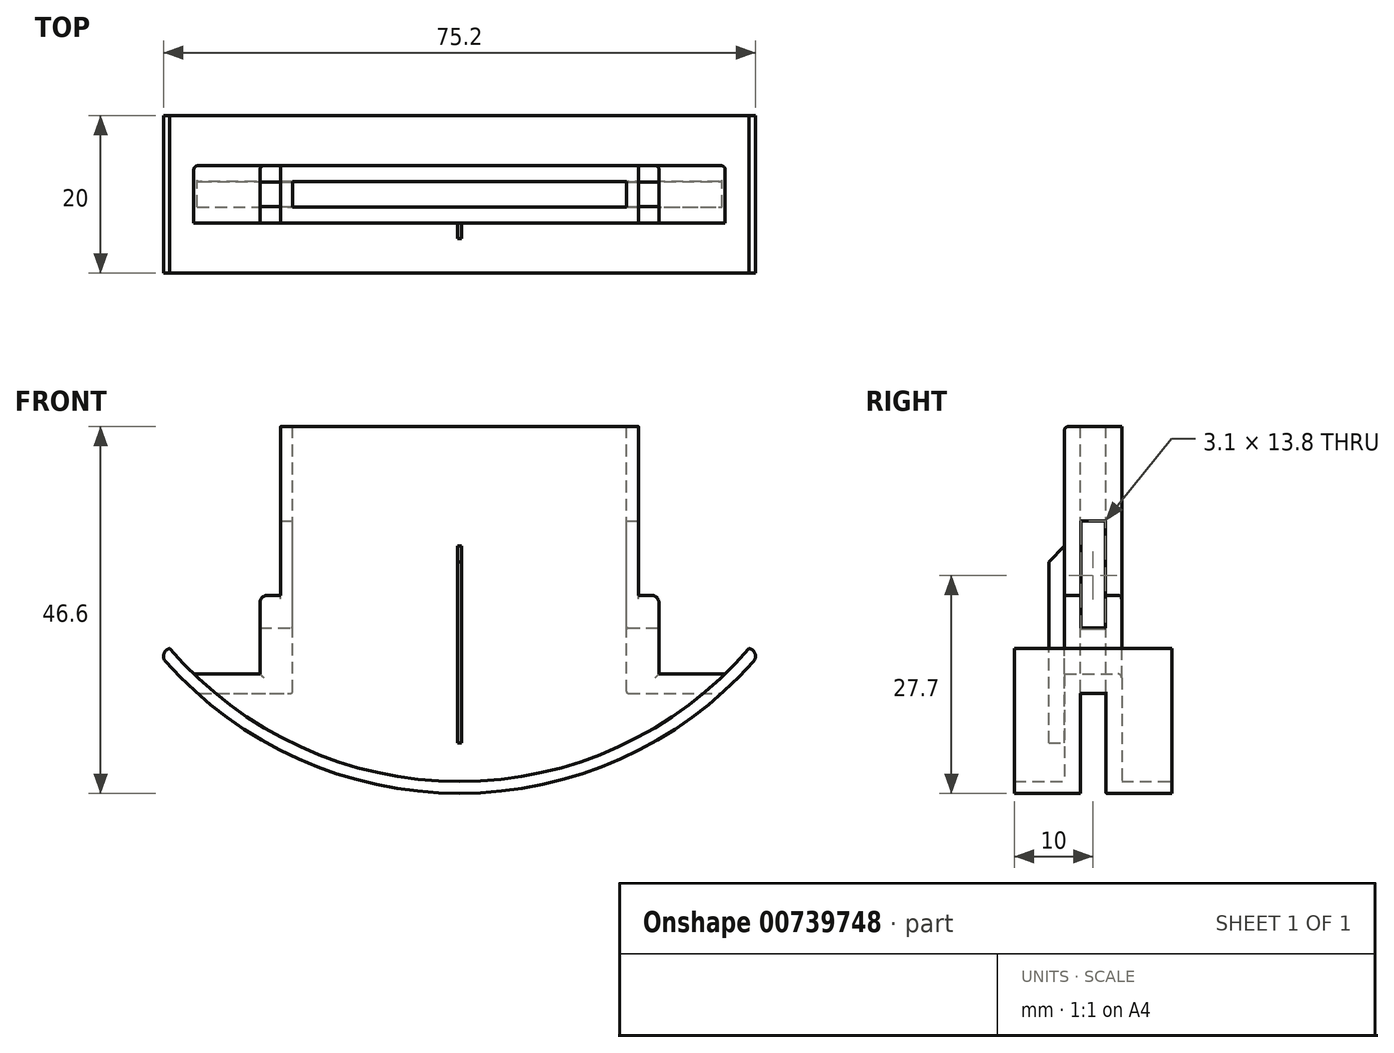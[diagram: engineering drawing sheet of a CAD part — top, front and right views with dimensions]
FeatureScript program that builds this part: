
annotation { "Feature Type Name" : "Feature", "Feature Type Description" : "" }
export const myFeature = defineFeature(function(context is Context, id is Id, definition is map)
    precondition{}
    {
        {
            var Q0;
            Q0=qCreatedBy(makeId("Front.planeOp"),FACE);
            var sketch = newSketch(context, id + "F0", { "sketchPlane" : qUnion([Q0])});
            skArc(sketch, "E0", {"start": v(-38.75, -31.6) * mm, "mid": v(0, -50) * mm, "end": v(38.75, -31.6) * mm});
            skArc(sketch, "E1", {"start": v(-36.8, -31.6) * mm, "mid": v(0, -48.5) * mm, "end": v(36.8, -31.6) * mm});
            skLineSegment(sketch, "E2", {"start": v(-38.75, -31.6) * mm, "end": v(-36.8, -31.6) * mm});
            skLineSegment(sketch, "E3.MirrorCS", {"start": v(38.75, -31.6) * mm, "end": v(36.8, -31.6) * mm});
            skSolve(sketch);
        }
        {
            var Q0;
            Q0 = qSketchRegion(id + "F0", true);
            extrude(context, id + "F1", {"entities" : qUnion([Q0]), "depth" : 20 * mm, "offsetDistance" : 25 * mm});
        }
        {
            var Q0;
            Q0=qCreatedBy(makeId("Top.planeOp"),FACE);
            var sketch = newSketch(context, id + "F2", { "sketchPlane" : qUnion([Q0])});
            skLineSegment(sketch, "E4", {"start": v(-40.45, -10) * mm, "end": v(40.4, -10) * mm, "construction": true});
            skLineSegment(sketch, "E5.bottom", {"start": v(-33.75, -6.37) * mm, "end": v(33.75, -6.37) * mm});
            skLineSegment(sketch, "E5.top", {"start": v(-33.75, -13.63) * mm, "end": v(33.75, -13.63) * mm});
            skLineSegment(sketch, "E5.left", {"start": v(-33.75, -6.37) * mm, "end": v(-33.75, -13.63) * mm});
            skLineSegment(sketch, "E5.right", {"start": v(33.75, -6.37) * mm, "end": v(33.75, -13.63) * mm});
            skSolve(sketch);
        }
        {
            var Q0;
            Q0 = qSketchRegion(id + "F2", true);
            extrude(context, id + "F3", {"entities" : qUnion([Q0]), "operationType" : NewBodyOperationType.ADD, "oppositeDirection" : true, "depth" : 48.69 * mm, "offsetDistance" : 25 * mm});
        }
        {
            var Q0;
            Q0=makeQuery(id+"F3.opExtrude","CAP_FACE",FACE,{"disambiguationData":[OSD([sQuery(id+"F2.wireOp",EDGE,"E5.bottom"),sQuery(id+"F2.wireOp",EDGE,"E5.top"),sQuery(id+"F2.wireOp",EDGE,"E5.left"),sQuery(id+"F2.wireOp",EDGE,"E5.right")])],"isStart":true});
            var sketch = newSketch(context, id + "F4", { "sketchPlane" : qUnion([Q0])});
            skLineSegment(sketch, "E6", {"start": v(-42.86, -10) * mm, "end": v(43.1, -10) * mm, "construction": true});
            skPoint(sketch, "E6.startSnap0", {"position": v(-33.75, -10) * mm});
            skLineSegment(sketch, "E7.0", {"start": v(-33.75, -6.37) * mm, "end": v(33.75, -6.37) * mm});
            skLineSegment(sketch, "E8.0", {"start": v(-36.8, 0) * mm, "end": v(36.8, 0) * mm});
            skLineSegment(sketch, "E9.bottom", {"start": v(-21.2, -8.4) * mm, "end": v(21.2, -8.4) * mm});
            skLineSegment(sketch, "E9.top", {"start": v(-21.2, -11.6) * mm, "end": v(21.2, -11.6) * mm});
            skLineSegment(sketch, "E9.left", {"start": v(-21.2, -8.4) * mm, "end": v(-21.2, -11.6) * mm});
            skLineSegment(sketch, "E9.right", {"start": v(21.2, -8.4) * mm, "end": v(21.2, -11.6) * mm});
            skSolve(sketch);
        }
        {
            var Q0;
            Q0 = qSketchRegion(id + "F4", true);
            extrude(context, id + "F5", {"entities" : qUnion([Q0]), "operationType" : NewBodyOperationType.REMOVE, "endBound" : BoundingType.THROUGH_ALL, "oppositeDirection" : true, "depth" : 25 * mm, "offsetDistance" : 25 * mm});
        }
        {
            var Q0;
            {var subQ0=sQuery(id+"F2.wireOp",EDGE,"E5.left");var subQ1=sQuery(id+"F2.wireOp",EDGE,"E5.bottom");Q0=makeQuery(id+"F3.boolean.opBoolean","SPLIT",FACE,{"disambiguationData":[TD([makeQuery(id+"F1.opExtrude","SWEPT_FACE",FACE,{"disambiguationData":[OSD([sQuery(id+"F0.wireOp",EDGE,"E0")])]}),makeQuery(id+"F3.opExtrude","CAP_FACE",FACE,{"disambiguationData":[OSD([subQ1,sQuery(id+"F2.wireOp",EDGE,"E5.top"),subQ0,sQuery(id+"F2.wireOp",EDGE,"E5.right")])],"isStart":false}),makeQuery(id+"F3.opExtrude","SWEPT_FACE",FACE,{"disambiguationData":[OSD([subQ0])]})])],"derivedFrom":makeQuery(id+"F3.opExtrude","SWEPT_FACE",FACE,{"disambiguationData":[OSD([subQ1])]})});}
            var sketch = newSketch(context, id + "F6", { "sketchPlane" : qUnion([Q0])});
            skLineSegment(sketch, "E10.0.0", {"start": v(33.75, -48.69) * mm, "end": v(33.75, -36.9) * mm});
            skArc(sketch, "E10.0.1", {"start": v(33.75, -36.9) * mm, "mid": v(23.32, -44.23) * mm, "end": v(11.37, -48.69) * mm});
            skLineSegment(sketch, "E10.0.2", {"start": v(11.37, -48.69) * mm, "end": v(33.75, -48.69) * mm});
            skLineSegment(sketch, "E11.0.0", {"start": v(-33.75, -48.69) * mm, "end": v(-11.37, -48.69) * mm});
            skArc(sketch, "E11.0.1", {"start": v(-11.37, -48.69) * mm, "mid": v(-23.32, -44.23) * mm, "end": v(-33.75, -36.9) * mm});
            skLineSegment(sketch, "E11.0.2", {"start": v(-33.75, -36.9) * mm, "end": v(-33.75, -48.69) * mm});
            skSolve(sketch);
        }
        {
            var Q0;
            Q0 = qSketchRegion(id + "F6", true);
            extrude(context, id + "F7", {"entities" : qUnion([Q0]), "operationType" : NewBodyOperationType.REMOVE, "endBound" : BoundingType.THROUGH_ALL, "oppositeDirection" : true, "depth" : 25 * mm, "offsetDistance" : 25 * mm});
        }
        {
            var Q0;
            {var subQ0=sQuery(id+"F2.wireOp",EDGE,"E5.right");var subQ1=sQuery(id+"F2.wireOp",EDGE,"E5.left");var subQ2=sQuery(id+"F2.wireOp",EDGE,"E5.bottom");Q0=makeQuery(id+"F3.boolean.opBoolean","SPLIT",FACE,{"disambiguationData":[TD([makeQuery(id+"F1.opExtrude","SWEPT_FACE",FACE,{"disambiguationData":[OSD([sQuery(id+"F0.wireOp",EDGE,"E1")])]}),makeQuery(id+"F3.opExtrude","CAP_FACE",FACE,{"disambiguationData":[OSD([subQ2,sQuery(id+"F2.wireOp",EDGE,"E5.top"),subQ1,subQ0])],"isStart":true}),makeQuery(id+"F3.opExtrude","SWEPT_FACE",FACE,{"disambiguationData":[OSD([subQ1])]}),makeQuery(id+"F3.opExtrude","SWEPT_FACE",FACE,{"disambiguationData":[OSD([subQ0])]})])],"derivedFrom":makeQuery(id+"F3.opExtrude","SWEPT_FACE",FACE,{"disambiguationData":[OSD([subQ2])]})});}
            var sketch = newSketch(context, id + "F8", { "sketchPlane" : qUnion([Q0])});
            skLineSegment(sketch, "E12.0", {"start": v(33.75, 0) * mm, "end": v(-33.75, 0) * mm});
            skArc(sketch, "E13.0", {"start": v(38.75, -31.6) * mm, "mid": v(0, -50) * mm, "end": v(-38.75, -31.6) * mm});
            skLineSegment(sketch, "E14.bottom", {"start": v(-33.75, 0) * mm, "end": v(33.75, 0) * mm});
            skLineSegment(sketch, "E14.top", {"start": v(-33.75, -3.4) * mm, "end": v(33.75, -3.4) * mm});
            skLineSegment(sketch, "E14.left", {"start": v(-33.75, 0) * mm, "end": v(-33.75, -3.4) * mm});
            skLineSegment(sketch, "E14.right", {"start": v(33.75, 0) * mm, "end": v(33.75, -3.4) * mm});
            skSolve(sketch);
        }
        {
            var Q0;
            Q0 = qSketchRegion(id + "F8", true);
            extrude(context, id + "F9", {"entities" : qUnion([Q0]), "operationType" : NewBodyOperationType.REMOVE, "endBound" : BoundingType.THROUGH_ALL, "oppositeDirection" : true, "depth" : 25 * mm, "offsetDistance" : 25 * mm});
        }
        {
            var Q0;
            {var subQ1=sQuery(id+"F2.wireOp",EDGE,"E5.right");Q0=makeQuery(id+"F3.boolean.opBoolean","SPLIT",FACE,{"disambiguationData":[TD([makeQuery(id+"F1.opExtrude","SWEPT_FACE",FACE,{"disambiguationData":[OSD([sQuery(id+"F0.wireOp",EDGE,"E1")])]})])],"derivedFrom":makeQuery(id+"F3.opExtrude","SWEPT_FACE",FACE,{"disambiguationData":[OSD([subQ1])]})});}
            var sketch = newSketch(context, id + "F10", { "sketchPlane" : qUnion([Q0])});
            skLineSegment(sketch, "E15.bottom", {"start": v(-11.55, -15.4) * mm, "end": v(-8.45, -15.4) * mm});
            skLineSegment(sketch, "E15.top", {"start": v(-11.55, -29) * mm, "end": v(-8.45, -29) * mm});
            skLineSegment(sketch, "E15.left", {"start": v(-11.55, -15.4) * mm, "end": v(-11.55, -29) * mm});
            skLineSegment(sketch, "E15.right", {"start": v(-8.45, -15.4) * mm, "end": v(-8.45, -29) * mm});
            skLineSegment(sketch, "E16.0", {"start": v(-13.63, -3.4) * mm, "end": v(-6.37, -3.4) * mm});
            skLineSegment(sketch, "E17.0", {"start": v(-13.63, -34.83) * mm, "end": v(-13.63, -3.4) * mm});
            skLineSegment(sketch, "E18.0", {"start": v(-6.37, -34.83) * mm, "end": v(-6.37, -3.4) * mm});
            skLineSegment(sketch, "E19", {"start": v(-10, -53.79) * mm, "end": v(-10, 8.71) * mm, "construction": true});
            skSolve(sketch);
        }
        {
            var Q0;
            Q0 = qSketchRegion(id + "F10", true);
            extrude(context, id + "F11", {"entities" : qUnion([Q0]), "operationType" : NewBodyOperationType.REMOVE, "endBound" : BoundingType.THROUGH_ALL, "oppositeDirection" : true, "depth" : 25 * mm, "offsetDistance" : 25 * mm});
        }
        {
            var Q0;
            {var subQ0=sQuery(id+"F2.wireOp",EDGE,"E5.right");var subQ1=sQuery(id+"F2.wireOp",EDGE,"E5.left");var subQ2=sQuery(id+"F2.wireOp",EDGE,"E5.top");Q0=makeQuery(id+"F3.boolean.opBoolean","SPLIT",FACE,{"disambiguationData":[TD([makeQuery(id+"F1.opExtrude","SWEPT_FACE",FACE,{"disambiguationData":[OSD([sQuery(id+"F0.wireOp",EDGE,"E1")])]}),makeQuery(id+"F3.opExtrude","CAP_FACE",FACE,{"disambiguationData":[OSD([sQuery(id+"F2.wireOp",EDGE,"E5.bottom"),subQ2,subQ1,subQ0])],"isStart":true}),makeQuery(id+"F3.opExtrude","SWEPT_FACE",FACE,{"disambiguationData":[OSD([subQ1])]}),makeQuery(id+"F3.opExtrude","SWEPT_FACE",FACE,{"disambiguationData":[OSD([subQ0])]})])],"derivedFrom":makeQuery(id+"F3.opExtrude","SWEPT_FACE",FACE,{"disambiguationData":[OSD([subQ2])]})});}
            var sketch = newSketch(context, id + "F12", { "sketchPlane" : qUnion([Q0])});
            skLineSegment(sketch, "E20.0", {"start": v(-33.75, -34.83) * mm, "end": v(-33.75, -3.4) * mm});
            skLineSegment(sketch, "E21", {"start": v(-33.75, -34.83) * mm, "end": v(-25.35, -34.83) * mm});
            skLineSegment(sketch, "E22", {"start": v(-25.35, -34.83) * mm, "end": v(-25.35, -24.83) * mm});
            skLineSegment(sketch, "E23", {"start": v(-25.35, -24.83) * mm, "end": v(-22.75, -24.83) * mm});
            skLineSegment(sketch, "E24", {"start": v(-22.75, -24.83) * mm, "end": v(-22.75, -3.4) * mm});
            skLineSegment(sketch, "E25", {"start": v(-33.75, -3.4) * mm, "end": v(-22.75, -3.4) * mm});
            skLineSegment(sketch, "E26.MirrorCS", {"start": v(33.75, -34.83) * mm, "end": v(33.75, -3.4) * mm});
            skLineSegment(sketch, "E27.MirrorCS", {"start": v(33.75, -34.83) * mm, "end": v(25.35, -34.83) * mm});
            skLineSegment(sketch, "E28.MirrorCS", {"start": v(25.35, -34.83) * mm, "end": v(25.35, -24.83) * mm});
            skLineSegment(sketch, "E29.MirrorCS", {"start": v(22.75, -24.83) * mm, "end": v(22.75, -3.4) * mm});
            skLineSegment(sketch, "E30.MirrorCS", {"start": v(25.35, -24.83) * mm, "end": v(22.75, -24.83) * mm});
            skLineSegment(sketch, "E31.MirrorCS", {"start": v(33.75, -3.4) * mm, "end": v(22.75, -3.4) * mm});
            skSolve(sketch);
        }
        {
            var Q0;
            Q0 = qSketchRegion(id + "F12", true);
            extrude(context, id + "F13", {"entities" : qUnion([Q0]), "operationType" : NewBodyOperationType.REMOVE, "endBound" : BoundingType.THROUGH_ALL, "oppositeDirection" : true, "depth" : 25 * mm, "offsetDistance" : 25 * mm});
        }
        {
            var Q0;
            Q0=qCreatedBy(makeId("Right.planeOp"),FACE);
            cPlane(context, id + "F14", {"entities" : qUnion([Q0]), "cplaneType" : CPlaneType.OFFSET, "offset" : 35 * mm, "width" : 150 * mm, "height" : 150 * mm});
        }
        {
            var Q0;
            Q0=qCreatedBy(id+"F14.planeOp",FACE);
            var sketch = newSketch(context, id + "F15", { "sketchPlane" : qUnion([Q0])});
            skPoint(sketch, "E32.0", {"position": v(-11.6, -45.28) * mm});
            skPoint(sketch, "E33.0", {"position": v(-8.4, -45.28) * mm});
            skLineSegment(sketch, "E34.bottom", {"start": v(-11.6, -45.28) * mm, "end": v(-8.4, -45.28) * mm});
            skLineSegment(sketch, "E34.top", {"start": v(-11.6, -37.28) * mm, "end": v(-8.4, -37.28) * mm});
            skLineSegment(sketch, "E34.left", {"start": v(-11.6, -45.28) * mm, "end": v(-11.6, -37.28) * mm});
            skLineSegment(sketch, "E34.right", {"start": v(-8.4, -45.28) * mm, "end": v(-8.4, -37.28) * mm});
            skSolve(sketch);
        }
        {
            var Q0;
            Q0 = qSketchRegion(id + "F15", true);
            extrude(context, id + "F16", {"entities" : qUnion([Q0]), "operationType" : NewBodyOperationType.REMOVE, "endBound" : BoundingType.THROUGH_ALL, "oppositeDirection" : true, "depth" : 25 * mm, "offsetDistance" : 25 * mm});
        }
        {
            var Q0;
            {var subQ0=sQuery(id+"F2.wireOp",EDGE,"E5.right");var subQ1=sQuery(id+"F2.wireOp",EDGE,"E5.left");var subQ2=sQuery(id+"F2.wireOp",EDGE,"E5.top");Q0=makeQuery(id+"F3.boolean.opBoolean","SPLIT",FACE,{"disambiguationData":[TD([makeQuery(id+"F1.opExtrude","SWEPT_FACE",FACE,{"disambiguationData":[OSD([sQuery(id+"F0.wireOp",EDGE,"E1")])]}),makeQuery(id+"F3.opExtrude","CAP_FACE",FACE,{"disambiguationData":[OSD([sQuery(id+"F2.wireOp",EDGE,"E5.bottom"),subQ2,subQ1,subQ0])],"isStart":true}),makeQuery(id+"F3.opExtrude","SWEPT_FACE",FACE,{"disambiguationData":[OSD([subQ1])]}),makeQuery(id+"F3.opExtrude","SWEPT_FACE",FACE,{"disambiguationData":[OSD([subQ0])]})])],"derivedFrom":makeQuery(id+"F3.opExtrude","SWEPT_FACE",FACE,{"disambiguationData":[OSD([subQ2])]})});}
            var sketch = newSketch(context, id + "F17", { "sketchPlane" : qUnion([Q0])});
            skLineSegment(sketch, "E35.bottom", {"start": v(-0.25, -43.58) * mm, "end": v(0.25, -43.58) * mm});
            skLineSegment(sketch, "E35.top", {"start": v(-0.25, -18.58) * mm, "end": v(0.25, -18.58) * mm});
            skLineSegment(sketch, "E35.left", {"start": v(-0.25, -43.58) * mm, "end": v(-0.25, -18.58) * mm});
            skLineSegment(sketch, "E35.right", {"start": v(0.25, -43.58) * mm, "end": v(0.25, -18.58) * mm});
            skSolve(sketch);
        }
        {
            var Q0;
            Q0 = qSketchRegion(id + "F17", true);
            extrude(context, id + "F18", {"entities" : qUnion([Q0]), "operationType" : NewBodyOperationType.ADD, "depth" : 2 * mm, "offsetDistance" : 25 * mm});
        }
        {
            var Q0;
            Q0=makeQuery(id+"F18.opExtrude","CAP_EDGE",EDGE,{"disambiguationData":[OSD([sQuery(id+"F17.wireOp",EDGE,"E35.top")])],"isStart":false});
            chamfer(context, id + "F19", {"entities" : qUnion([Q0]), "width" : 2 * mm, "tangentPropagation" : true});
        }
        {
            var Q0;
            Q0=makeQuery(id+"F13.boolean.opBoolean","COPY",EDGE,{"derivedFrom":makeQuery(id+"F13.opExtrude","SWEPT_EDGE",EDGE,{"disambiguationData":[OSD([sQuery(id+"F2.wireOp",EDGE,"E5.top"),sQuery(id+"F8.wireOp",EDGE,"E14.top"),sQuery(id+"F12.wireOp",EDGE,"E29.MirrorCS"),sQuery(id+"F12.wireOp",EDGE,"E31.MirrorCS")])]})});
            var Q1;
            Q1=makeQuery(id+"F13.boolean.opBoolean","COPY",EDGE,{"derivedFrom":makeQuery(id+"F13.opExtrude","SWEPT_EDGE",EDGE,{"disambiguationData":[OSD([sQuery(id+"F2.wireOp",EDGE,"E5.top"),sQuery(id+"F8.wireOp",EDGE,"E14.top"),sQuery(id+"F12.wireOp",EDGE,"E24"),sQuery(id+"F12.wireOp",EDGE,"E25")])]})});
            var Q2;
            {var subQ0=sQuery(id+"F12.wireOp",EDGE,"E28.MirrorCS");var subQ1=sQuery(id+"F12.wireOp",EDGE,"E30.MirrorCS");Q2=makeQuery(id+"F13.boolean.opBoolean","COPY",EDGE,{"disambiguationData":[TD([makeQuery(id+"F3.opExtrude","SWEPT_FACE",FACE,{"disambiguationData":[OSD([sQuery(id+"F2.wireOp",EDGE,"E5.bottom")])]})])],"derivedFrom":makeQuery(id+"F13.opExtrude","SWEPT_EDGE",EDGE,{"disambiguationData":[OSD([subQ0,subQ1])]})});}
            var Q3;
            {var subQ0=sQuery(id+"F12.wireOp",EDGE,"E28.MirrorCS");var subQ1=sQuery(id+"F12.wireOp",EDGE,"E30.MirrorCS");Q3=makeQuery(id+"F13.boolean.opBoolean","COPY",EDGE,{"disambiguationData":[TD([makeQuery(id+"F3.opExtrude","SWEPT_FACE",FACE,{"disambiguationData":[OSD([sQuery(id+"F2.wireOp",EDGE,"E5.top")])]})])],"derivedFrom":makeQuery(id+"F13.opExtrude","SWEPT_EDGE",EDGE,{"disambiguationData":[OSD([subQ0,subQ1])]})});}
            var Q4;
            {var subQ0=sQuery(id+"F12.wireOp",EDGE,"E23");var subQ1=sQuery(id+"F12.wireOp",EDGE,"E22");Q4=makeQuery(id+"F13.boolean.opBoolean","COPY",EDGE,{"disambiguationData":[TD([makeQuery(id+"F3.opExtrude","SWEPT_FACE",FACE,{"disambiguationData":[OSD([sQuery(id+"F2.wireOp",EDGE,"E5.bottom")])]})])],"derivedFrom":makeQuery(id+"F13.opExtrude","SWEPT_EDGE",EDGE,{"disambiguationData":[OSD([subQ1,subQ0])]})});}
            var Q5;
            {var subQ0=sQuery(id+"F12.wireOp",EDGE,"E22");var subQ1=sQuery(id+"F12.wireOp",EDGE,"E23");Q5=makeQuery(id+"F13.boolean.opBoolean","COPY",EDGE,{"disambiguationData":[TD([makeQuery(id+"F3.opExtrude","SWEPT_FACE",FACE,{"disambiguationData":[OSD([sQuery(id+"F2.wireOp",EDGE,"E5.top")])]})])],"derivedFrom":makeQuery(id+"F13.opExtrude","SWEPT_EDGE",EDGE,{"disambiguationData":[OSD([subQ0,subQ1])]})});}
            var Q6;
            Q6=makeQuery(id+"F1.opExtrude","SWEPT_EDGE",EDGE,{"disambiguationData":[OSD([sQuery(id+"F0.wireOp",EDGE,"E0"),sQuery(id+"F0.wireOp",EDGE,"E2")])]});
            var Q7;
            Q7=makeQuery(id+"F1.opExtrude","SWEPT_EDGE",EDGE,{"disambiguationData":[OSD([sQuery(id+"F0.wireOp",EDGE,"E0"),sQuery(id+"F0.wireOp",EDGE,"E3.MirrorCS")])]});
            fillet(context, id + "F20", {"entities" : qUnion([Q0, Q1, Q2, Q3, Q4, Q5, Q6, Q7]), "radius" : 1 * mm, "tangentPropagation" : true, "allowEdgeOverflow" : false});
        }
        {
            var Q0;
            Q0=makeQuery(id+"F9.boolean.opBoolean","COPY",EDGE,{"derivedFrom":makeQuery(id+"F9.opExtrude","CAP_EDGE",EDGE,{"disambiguationData":[OSD([sQuery(id+"F8.wireOp",EDGE,"E14.top")])],"isStart":true})});
            var Q1;
            {var subQ0=sQuery(id+"F2.wireOp",EDGE,"E5.right");var subQ1=sQuery(id+"F2.wireOp",EDGE,"E5.left");var subQ2=sQuery(id+"F2.wireOp",EDGE,"E5.top");Q1=makeQuery(id+"F9.boolean.opBoolean","INTERSECT",EDGE,{"derivedFrom":[makeQuery(id+"F3.boolean.opBoolean","SPLIT",FACE,{"disambiguationData":[TD([makeQuery(id+"F1.opExtrude","SWEPT_FACE",FACE,{"disambiguationData":[OSD([sQuery(id+"F0.wireOp",EDGE,"E1")])]}),makeQuery(id+"F3.opExtrude","CAP_FACE",FACE,{"disambiguationData":[OSD([sQuery(id+"F2.wireOp",EDGE,"E5.bottom"),subQ2,subQ1,subQ0])],"isStart":true}),makeQuery(id+"F3.opExtrude","SWEPT_FACE",FACE,{"disambiguationData":[OSD([subQ1])]}),makeQuery(id+"F3.opExtrude","SWEPT_FACE",FACE,{"disambiguationData":[OSD([subQ0])]})])],"derivedFrom":makeQuery(id+"F3.opExtrude","SWEPT_FACE",FACE,{"disambiguationData":[OSD([subQ2])]})}),makeQuery(id+"F9.opExtrude","SWEPT_FACE",FACE,{"disambiguationData":[OSD([sQuery(id+"F8.wireOp",EDGE,"E14.top")])]})]});}
            var Q2;
            Q2=makeQuery(id+"F13.boolean.opBoolean","COPY",EDGE,{"derivedFrom":makeQuery(id+"F13.opExtrude","CAP_EDGE",EDGE,{"disambiguationData":[OSD([sQuery(id+"F12.wireOp",EDGE,"E28.MirrorCS")])],"isStart":true})});
            var Q3;
            {var subQ0=sQuery(id+"F2.wireOp",EDGE,"E5.right");var subQ1=sQuery(id+"F2.wireOp",EDGE,"E5.left");var subQ2=sQuery(id+"F2.wireOp",EDGE,"E5.bottom");Q3=makeQuery(id+"F13.boolean.opBoolean","INTERSECT",EDGE,{"derivedFrom":[makeQuery(id+"F3.boolean.opBoolean","SPLIT",FACE,{"disambiguationData":[TD([makeQuery(id+"F1.opExtrude","SWEPT_FACE",FACE,{"disambiguationData":[OSD([sQuery(id+"F0.wireOp",EDGE,"E1")])]}),makeQuery(id+"F3.opExtrude","CAP_FACE",FACE,{"disambiguationData":[OSD([subQ2,sQuery(id+"F2.wireOp",EDGE,"E5.top"),subQ1,subQ0])],"isStart":true}),makeQuery(id+"F3.opExtrude","SWEPT_FACE",FACE,{"disambiguationData":[OSD([subQ1])]}),makeQuery(id+"F3.opExtrude","SWEPT_FACE",FACE,{"disambiguationData":[OSD([subQ0])]})])],"derivedFrom":makeQuery(id+"F3.opExtrude","SWEPT_FACE",FACE,{"disambiguationData":[OSD([subQ2])]})}),makeQuery(id+"F13.opExtrude","SWEPT_FACE",FACE,{"disambiguationData":[OSD([sQuery(id+"F12.wireOp",EDGE,"E28.MirrorCS")])]})]});}
            var Q4;
            Q4=makeQuery(id+"F13.boolean.opBoolean","COPY",EDGE,{"derivedFrom":makeQuery(id+"F13.opExtrude","CAP_EDGE",EDGE,{"disambiguationData":[OSD([sQuery(id+"F12.wireOp",EDGE,"E27.MirrorCS")])],"isStart":true})});
            var Q5;
            {var subQ0=sQuery(id+"F2.wireOp",EDGE,"E5.right");var subQ1=sQuery(id+"F2.wireOp",EDGE,"E5.left");var subQ2=sQuery(id+"F2.wireOp",EDGE,"E5.bottom");Q5=makeQuery(id+"F13.boolean.opBoolean","INTERSECT",EDGE,{"derivedFrom":[makeQuery(id+"F3.boolean.opBoolean","SPLIT",FACE,{"disambiguationData":[TD([makeQuery(id+"F1.opExtrude","SWEPT_FACE",FACE,{"disambiguationData":[OSD([sQuery(id+"F0.wireOp",EDGE,"E1")])]}),makeQuery(id+"F3.opExtrude","CAP_FACE",FACE,{"disambiguationData":[OSD([subQ2,sQuery(id+"F2.wireOp",EDGE,"E5.top"),subQ1,subQ0])],"isStart":true}),makeQuery(id+"F3.opExtrude","SWEPT_FACE",FACE,{"disambiguationData":[OSD([subQ1])]}),makeQuery(id+"F3.opExtrude","SWEPT_FACE",FACE,{"disambiguationData":[OSD([subQ0])]})])],"derivedFrom":makeQuery(id+"F3.opExtrude","SWEPT_FACE",FACE,{"disambiguationData":[OSD([subQ2])]})}),makeQuery(id+"F13.opExtrude","SWEPT_FACE",FACE,{"disambiguationData":[OSD([sQuery(id+"F12.wireOp",EDGE,"E27.MirrorCS")])]})]});}
            var Q6;
            Q6=makeQuery(id+"F13.boolean.opBoolean","COPY",EDGE,{"derivedFrom":makeQuery(id+"F13.opExtrude","CAP_EDGE",EDGE,{"disambiguationData":[OSD([sQuery(id+"F12.wireOp",EDGE,"E22")])],"isStart":true})});
            var Q7;
            {var subQ0=sQuery(id+"F2.wireOp",EDGE,"E5.right");var subQ1=sQuery(id+"F2.wireOp",EDGE,"E5.left");var subQ2=sQuery(id+"F2.wireOp",EDGE,"E5.bottom");Q7=makeQuery(id+"F13.boolean.opBoolean","INTERSECT",EDGE,{"derivedFrom":[makeQuery(id+"F3.boolean.opBoolean","SPLIT",FACE,{"disambiguationData":[TD([makeQuery(id+"F1.opExtrude","SWEPT_FACE",FACE,{"disambiguationData":[OSD([sQuery(id+"F0.wireOp",EDGE,"E1")])]}),makeQuery(id+"F3.opExtrude","CAP_FACE",FACE,{"disambiguationData":[OSD([subQ2,sQuery(id+"F2.wireOp",EDGE,"E5.top"),subQ1,subQ0])],"isStart":true}),makeQuery(id+"F3.opExtrude","SWEPT_FACE",FACE,{"disambiguationData":[OSD([subQ1])]}),makeQuery(id+"F3.opExtrude","SWEPT_FACE",FACE,{"disambiguationData":[OSD([subQ0])]})])],"derivedFrom":makeQuery(id+"F3.opExtrude","SWEPT_FACE",FACE,{"disambiguationData":[OSD([subQ2])]})}),makeQuery(id+"F13.opExtrude","SWEPT_FACE",FACE,{"disambiguationData":[OSD([sQuery(id+"F12.wireOp",EDGE,"E22")])]})]});}
            var Q8;
            Q8=makeQuery(id+"F13.boolean.opBoolean","COPY",EDGE,{"derivedFrom":makeQuery(id+"F13.opExtrude","CAP_EDGE",EDGE,{"disambiguationData":[OSD([sQuery(id+"F12.wireOp",EDGE,"E21")])],"isStart":true})});
            var Q9;
            {var subQ0=sQuery(id+"F2.wireOp",EDGE,"E5.right");var subQ1=sQuery(id+"F2.wireOp",EDGE,"E5.left");var subQ2=sQuery(id+"F2.wireOp",EDGE,"E5.bottom");Q9=makeQuery(id+"F13.boolean.opBoolean","INTERSECT",EDGE,{"derivedFrom":[makeQuery(id+"F3.boolean.opBoolean","SPLIT",FACE,{"disambiguationData":[TD([makeQuery(id+"F1.opExtrude","SWEPT_FACE",FACE,{"disambiguationData":[OSD([sQuery(id+"F0.wireOp",EDGE,"E1")])]}),makeQuery(id+"F3.opExtrude","CAP_FACE",FACE,{"disambiguationData":[OSD([subQ2,sQuery(id+"F2.wireOp",EDGE,"E5.top"),subQ1,subQ0])],"isStart":true}),makeQuery(id+"F3.opExtrude","SWEPT_FACE",FACE,{"disambiguationData":[OSD([subQ1])]}),makeQuery(id+"F3.opExtrude","SWEPT_FACE",FACE,{"disambiguationData":[OSD([subQ0])]})])],"derivedFrom":makeQuery(id+"F3.opExtrude","SWEPT_FACE",FACE,{"disambiguationData":[OSD([subQ2])]})}),makeQuery(id+"F13.opExtrude","SWEPT_FACE",FACE,{"disambiguationData":[OSD([sQuery(id+"F12.wireOp",EDGE,"E21")])]})]});}
            fillet(context, id + "F21", {"entities" : qUnion([Q0, Q1, Q2, Q3, Q4, Q5, Q6, Q7, Q8, Q9]), "radius" : .5 * mm, "tangentPropagation" : true, "allowEdgeOverflow" : false});
        }
        {
            var Q0;
            Q0=makeQuery(id+"F7.boolean.opBoolean","INTERSECT",EDGE,{"derivedFrom":[makeQuery(id+"F5.boolean.opBoolean","COPY",FACE,{"derivedFrom":makeQuery(id+"F5.opExtrude","SWEPT_FACE",FACE,{"disambiguationData":[OSD([sQuery(id+"F4.wireOp",EDGE,"E9.bottom")])]})}),makeQuery(id+"F7.opExtrude","SWEPT_FACE",FACE,{"disambiguationData":[OSD([sQuery(id+"F6.wireOp",EDGE,"E10.0.1")])]}),makeQuery(id+"F7.opExtrude","SWEPT_FACE",FACE,{"disambiguationData":[OSD([sQuery(id+"F6.wireOp",EDGE,"E11.0.1")])]})]});
            var Q1;
            Q1=makeQuery(id+"F11.boolean.opBoolean","INTERSECT",EDGE,{"derivedFrom":[makeQuery(id+"F5.boolean.opBoolean","COPY",FACE,{"derivedFrom":makeQuery(id+"F5.opExtrude","SWEPT_FACE",FACE,{"disambiguationData":[OSD([sQuery(id+"F4.wireOp",EDGE,"E9.right")])]})}),makeQuery(id+"F11.opExtrude","SWEPT_FACE",FACE,{"disambiguationData":[OSD([sQuery(id+"F10.wireOp",EDGE,"E15.top")])]})]});
            var Q2;
            Q2=makeQuery(id+"F11.boolean.opBoolean","INTERSECT",EDGE,{"derivedFrom":[makeQuery(id+"F5.boolean.opBoolean","COPY",FACE,{"derivedFrom":makeQuery(id+"F5.opExtrude","SWEPT_FACE",FACE,{"disambiguationData":[OSD([sQuery(id+"F4.wireOp",EDGE,"E9.left")])]})}),makeQuery(id+"F11.opExtrude","SWEPT_FACE",FACE,{"disambiguationData":[OSD([sQuery(id+"F10.wireOp",EDGE,"E15.top")])]})]});
            var Q3;
            Q3=makeQuery(id+"F16.boolean.opBoolean","INTERSECT",EDGE,{"derivedFrom":[makeQuery(id+"F5.boolean.opBoolean","COPY",FACE,{"derivedFrom":makeQuery(id+"F5.opExtrude","SWEPT_FACE",FACE,{"disambiguationData":[OSD([sQuery(id+"F4.wireOp",EDGE,"E9.right")])]})}),makeQuery(id+"F16.opExtrude","SWEPT_FACE",FACE,{"disambiguationData":[OSD([sQuery(id+"F15.wireOp",EDGE,"E34.top")])]})]});
            var Q4;
            Q4=makeQuery(id+"F16.boolean.opBoolean","INTERSECT",EDGE,{"derivedFrom":[makeQuery(id+"F5.boolean.opBoolean","COPY",FACE,{"derivedFrom":makeQuery(id+"F5.opExtrude","SWEPT_FACE",FACE,{"disambiguationData":[OSD([sQuery(id+"F4.wireOp",EDGE,"E9.left")])]})}),makeQuery(id+"F16.opExtrude","SWEPT_FACE",FACE,{"disambiguationData":[OSD([sQuery(id+"F15.wireOp",EDGE,"E34.top")])]})]});
            fillet(context, id + "F22", {"entities" : qUnion([Q0, Q1, Q2, Q3, Q4]), "radius" : .2 * mm, "tangentPropagation" : true, "allowEdgeOverflow" : false});
        }
    });
